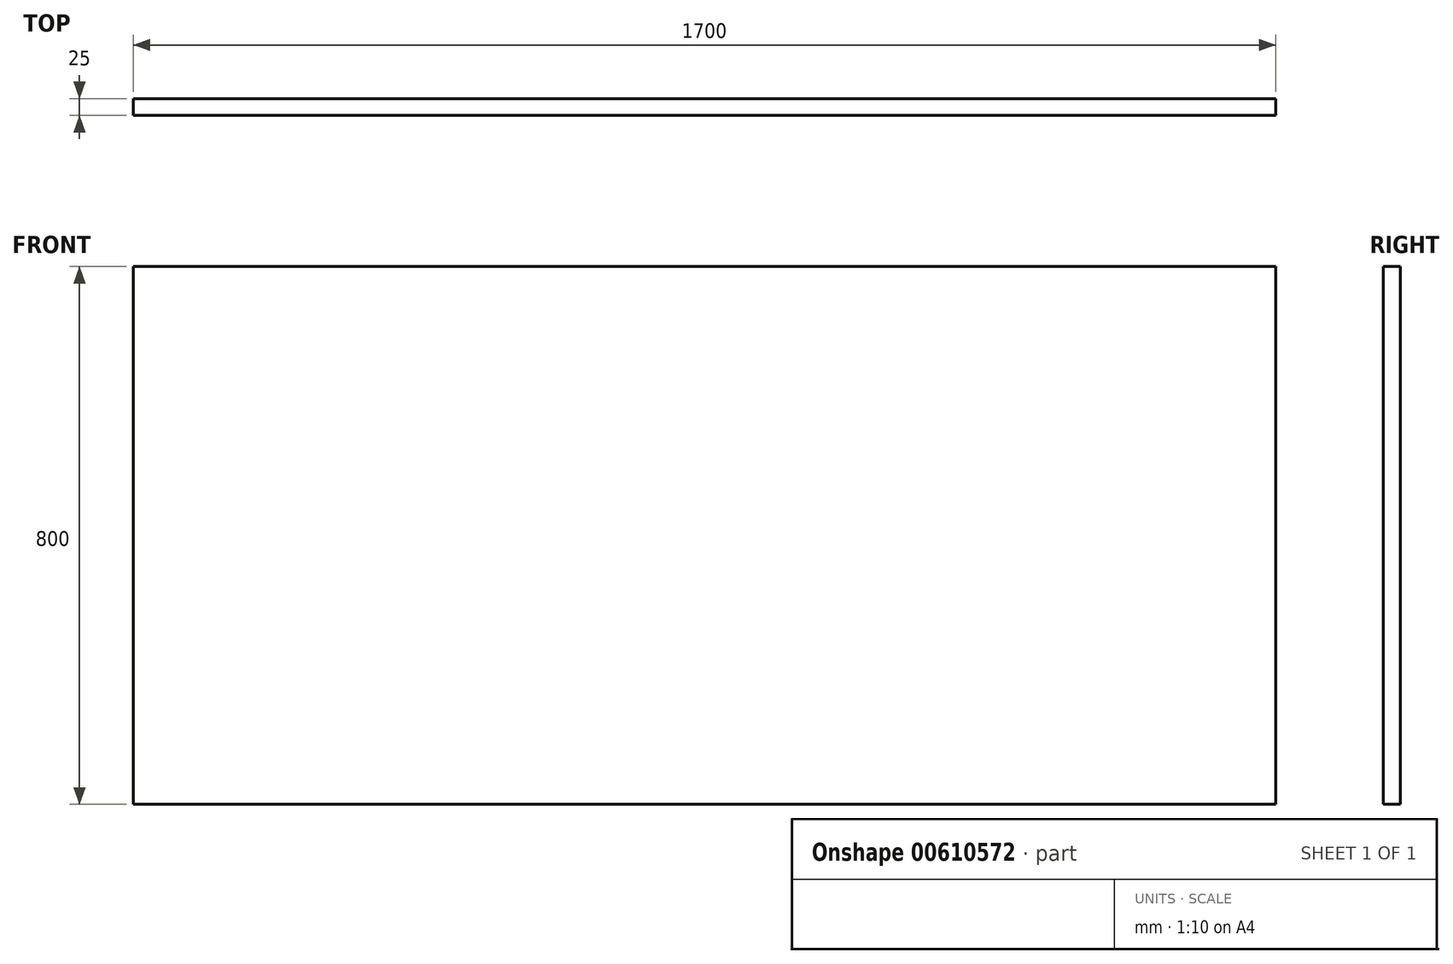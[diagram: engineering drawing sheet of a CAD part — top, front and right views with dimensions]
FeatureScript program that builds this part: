
annotation { "Feature Type Name" : "Feature", "Feature Type Description" : "" }
export const myFeature = defineFeature(function(context is Context, id is Id, definition is map)
    precondition{}
    {
        {
            var Q0;
            Q0=qCreatedBy(makeId("Front.planeOp"),FACE);
            var sketch = newSketch(context, id + "F0", { "sketchPlane" : qUnion([Q0])});
            skLineSegment(sketch, "E0.bottom", {"start": v(-850, 400) * mm, "end": v(850, 400) * mm});
            skLineSegment(sketch, "E0.top", {"start": v(-850, -400) * mm, "end": v(850, -400) * mm});
            skLineSegment(sketch, "E0.left", {"start": v(-850, 400) * mm, "end": v(-850, -400) * mm});
            skLineSegment(sketch, "E0.right", {"start": v(850, 400) * mm, "end": v(850, -400) * mm});
            skPoint(sketch, "E0.middle", {"position": v(0, 0) * mm});
            skSolve(sketch);
        }
        {
            var Q0;
            Q0 = qSketchRegion(id + "F0", true);
            extrude(context, id + "F1", {"entities" : qUnion([Q0]), "depth" : 25 * mm, "offsetDistance" : 25 * mm});
        }
    });
